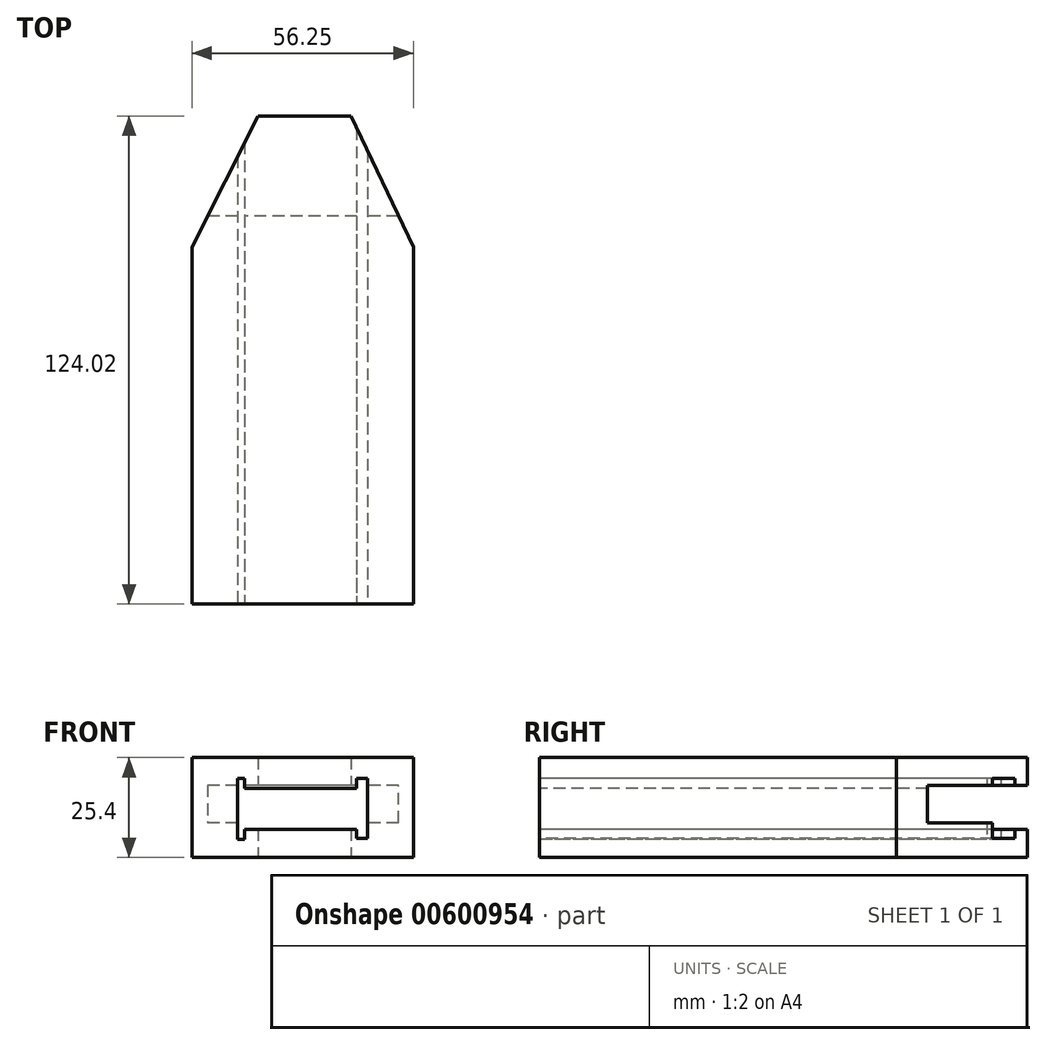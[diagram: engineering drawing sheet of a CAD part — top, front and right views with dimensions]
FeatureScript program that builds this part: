
annotation { "Feature Type Name" : "Feature", "Feature Type Description" : "" }
export const myFeature = defineFeature(function(context is Context, id is Id, definition is map)
    precondition{}
    {
        {
            var Q0;
            Q0=qCreatedBy(makeId("Top.planeOp"),FACE);
            var sketch = newSketch(context, id + "F0", { "sketchPlane" : qUnion([Q0])});
            skLineSegment(sketch, "E0", {"start": v(-10.2, 0) * mm, "end": v(13.38, 0) * mm});
            skLineSegment(sketch, "E1", {"start": v(13.38, 0) * mm, "end": v(29.26, -33.34) * mm});
            skLineSegment(sketch, "E2", {"start": v(29.26, -33.34) * mm, "end": v(-27, -33.34) * mm});
            skLineSegment(sketch, "E3", {"start": v(-27, -33.34) * mm, "end": v(-10.2, 0) * mm});
            skSolve(sketch);
        }
        {
            var Q0;
            Q0 = qSketchRegion(id + "F0", true);
            extrude(context, id + "F1", {"entities" : qUnion([Q0]), "depth" : 25.4 * mm, "offsetDistance" : 25.4 * mm});
        }
        {
            var Q0;
            Q0=makeQuery(id+"F1.opExtrude","SWEPT_FACE",FACE,{"disambiguationData":[OSD([sQuery(id+"F0.wireOp",EDGE,"E0")])]});
            var sketch = newSketch(context, id + "F2", { "sketchPlane" : qUnion([Q0])});
            skLineSegment(sketch, "E4.bottom", {"start": v(-38.56, 18.37) * mm, "end": v(33.11, 18.37) * mm});
            skLineSegment(sketch, "E4.top", {"start": v(-38.56, 8.84) * mm, "end": v(33.11, 8.84) * mm});
            skLineSegment(sketch, "E4.left", {"start": v(-38.56, 18.37) * mm, "end": v(-38.56, 8.84) * mm});
            skLineSegment(sketch, "E4.right", {"start": v(33.11, 18.37) * mm, "end": v(33.11, 8.84) * mm});
            skSolve(sketch);
        }
        {
            var Q0;
            Q0 = qSketchRegion(id + "F2", true);
            extrude(context, id + "F3", {"entities" : qUnion([Q0]), "operationType" : NewBodyOperationType.REMOVE, "oppositeDirection" : true, "depth" : 25.4 * mm, "offsetDistance" : 25.4 * mm});
        }
        {
            var Q0;
            Q0=makeQuery(id+"F1.opExtrude","SWEPT_FACE",FACE,{"disambiguationData":[OSD([sQuery(id+"F0.wireOp",EDGE,"E2")])]});
            extrude(context, id + "F4", {"entities" : qUnion([Q0]), "operationType" : NewBodyOperationType.ADD, "depth" : 90.68 * mm, "offsetDistance" : 25.4 * mm});
        }
        {
            var Q0;
            Q0=makeQuery(id+"F4.opExtrude","CAP_FACE",FACE,{"disambiguationData":[OSD([sQuery(id+"F0.wireOp",EDGE,"E2")])],"isStart":false});
            var sketch = newSketch(context, id + "F5", { "sketchPlane" : qUnion([Q0])});
            skLineSegment(sketch, "E5.bottom", {"start": v(17.63, 7.18) * mm, "end": v(-15.4, 7.18) * mm});
            skLineSegment(sketch, "E5.top", {"start": v(17.63, 17.6) * mm, "end": v(-15.4, 17.6) * mm});
            skLineSegment(sketch, "E5.left", {"start": v(17.63, 7.18) * mm, "end": v(17.63, 17.6) * mm});
            skLineSegment(sketch, "E5.right", {"start": v(-15.4, 7.18) * mm, "end": v(-15.4, 17.6) * mm});
            skLineSegment(sketch, "E6.bottom", {"start": v(17.63, 4.9) * mm, "end": v(14.88, 4.9) * mm});
            skLineSegment(sketch, "E6.top", {"start": v(17.63, 20.13) * mm, "end": v(14.88, 20.13) * mm});
            skLineSegment(sketch, "E6.left", {"start": v(17.63, 4.9) * mm, "end": v(17.63, 20.13) * mm});
            skLineSegment(sketch, "E6.right", {"start": v(14.88, 4.9) * mm, "end": v(14.88, 20.13) * mm});
            skLineSegment(sketch, "E7.bottom", {"start": v(-15.4, 4.65) * mm, "end": v(-13.59, 4.65) * mm});
            skLineSegment(sketch, "E7.top", {"start": v(-15.4, 20.13) * mm, "end": v(-13.59, 20.13) * mm});
            skLineSegment(sketch, "E7.left", {"start": v(-15.4, 4.65) * mm, "end": v(-15.4, 20.13) * mm});
            skLineSegment(sketch, "E7.right", {"start": v(-13.59, 4.65) * mm, "end": v(-13.59, 20.13) * mm});
            skSolve(sketch);
        }
        {
            var Q0;
            Q0 = qSketchRegion(id + "F5", true);
            extrude(context, id + "F6", {"entities" : qUnion([Q0]), "operationType" : NewBodyOperationType.REMOVE, "oppositeDirection" : true, "depth" : 254 * mm, "offsetDistance" : 25.4 * mm});
        }
    });
